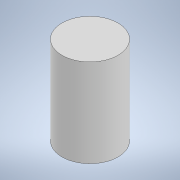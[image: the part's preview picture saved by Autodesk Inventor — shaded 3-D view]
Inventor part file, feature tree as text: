
AUTODESK INVENTOR PART (.ipt)
format: ipt  version: 2021 (Build 250183000, 183)  size: 88,576 bytes
history: native  units: mm
features: extrude x1, sketch x1
ambient origin geometry x8: Origin, YZ Plane, XZ Plane, XY Plane, X Axis, Y Axis, Z Axis, Center Point
bodies: Solid1 (feature_tree)
feature tree (2):
  extrude  "Extrusion1"  Depth=5.0mm TaperAngle=0.0deg
  sketch  "Sketch1"  dims[d0=3.175mm d1=5.0mm d2=0.0mm]
